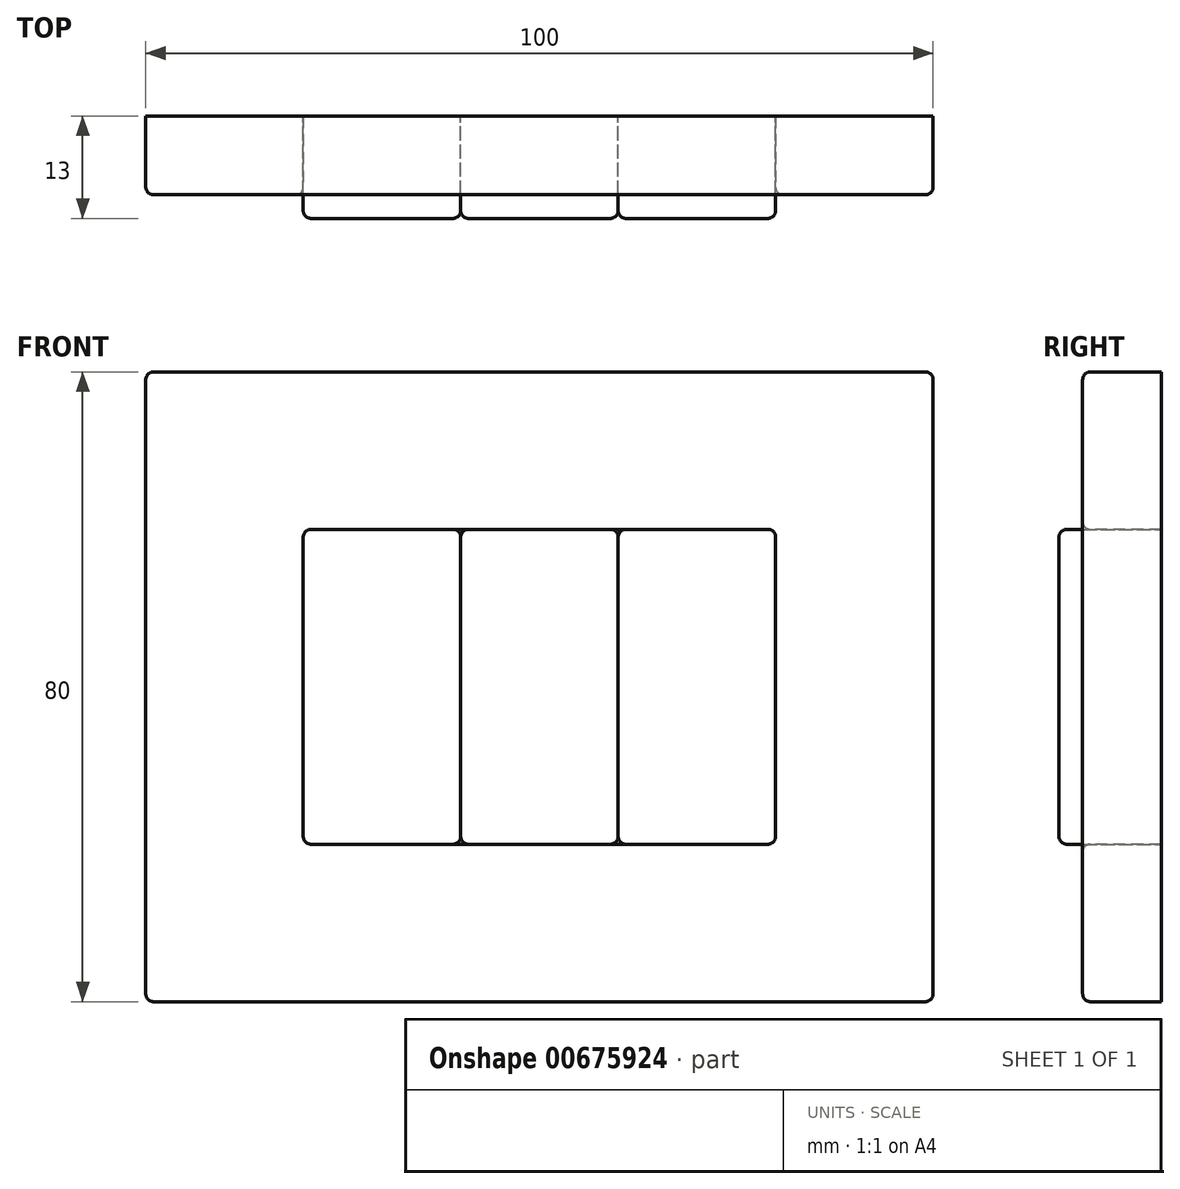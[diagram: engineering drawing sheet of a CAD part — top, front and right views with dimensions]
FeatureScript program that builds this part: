
annotation { "Feature Type Name" : "Feature", "Feature Type Description" : "" }
export const myFeature = defineFeature(function(context is Context, id is Id, definition is map)
    precondition{}
    {
        {
            var Q0;
            Q0=qCreatedBy(makeId("Front.planeOp"),FACE);
            var sketch = newSketch(context, id + "F0", { "sketchPlane" : qUnion([Q0])});
            skLineSegment(sketch, "E0.bottom", {"start": v(0, 0) * mm, "end": v(100, 0) * mm});
            skLineSegment(sketch, "E0.top", {"start": v(0, 80) * mm, "end": v(100, 80) * mm});
            skLineSegment(sketch, "E0.left", {"start": v(0, 0) * mm, "end": v(0, 80) * mm});
            skLineSegment(sketch, "E0.right", {"start": v(100, 0) * mm, "end": v(100, 80) * mm});
            skLineSegment(sketch, "E1.bottom", {"start": v(20, 60) * mm, "end": v(40, 60) * mm});
            skLineSegment(sketch, "E1.top", {"start": v(20, 20) * mm, "end": v(40, 20) * mm});
            skLineSegment(sketch, "E1.left", {"start": v(20, 60) * mm, "end": v(20, 20) * mm});
            skLineSegment(sketch, "E1.right", {"start": v(40, 60) * mm, "end": v(40, 20) * mm});
            skLineSegment(sketch, "E2.bottom", {"start": v(40, 60) * mm, "end": v(60, 60) * mm});
            skLineSegment(sketch, "E2.top", {"start": v(40, 20) * mm, "end": v(60, 20) * mm});
            skLineSegment(sketch, "E2.right", {"start": v(60, 60) * mm, "end": v(60, 20) * mm});
            skLineSegment(sketch, "E3.bottom", {"start": v(60, 60) * mm, "end": v(80, 60) * mm});
            skLineSegment(sketch, "E3.top", {"start": v(60, 20) * mm, "end": v(80, 20) * mm});
            skLineSegment(sketch, "E3.right", {"start": v(80, 60) * mm, "end": v(80, 20) * mm});
            skLineSegment(sketch, "E4", {"start": v(20, 40) * mm, "end": v(0, 40) * mm, "construction": true});
            skLineSegment(sketch, "E5", {"start": v(50, 60) * mm, "end": v(50, 80) * mm, "construction": true});
            skSolve(sketch);
        }
        {
            var Q0;
            Q0=makeQuery(id+"F0.imprint","IMPRINT",FACE,{"disambiguationData":[TD([[makeQuery(id+"F0.imprint","IMPRINT",EDGE,{"derivedFrom":sQuery(id+"F0.wireOp",EDGE,"E1.bottom")}),-1.0]])]});
            var Q1;
            Q1=makeQuery(id+"F0.imprint","IMPRINT",FACE,{"disambiguationData":[TD([[makeQuery(id+"F0.imprint","IMPRINT",EDGE,{"derivedFrom":sQuery(id+"F0.wireOp",EDGE,"E3.bottom")}),-1.0]])]});
            extrude(context, id + "F1", {"entities" : qUnion([Q0, Q1]), "depth" : 3 * mm, "offsetDistance" : 25 * mm, "hasSecondDirection" : true, "secondDirectionOppositeDirection" : true, "secondDirectionDepth" : 10 * mm});
        }
        {
            var Q0;
            Q0=makeQuery(id+"F0.imprint","IMPRINT",FACE,{"disambiguationData":[TD([[makeQuery(id+"F0.imprint","IMPRINT",EDGE,{"derivedFrom":sQuery(id+"F0.wireOp",EDGE,"E2.bottom")}),-1.0]])]});
            extrude(context, id + "F2", {"entities" : qUnion([Q0]), "depth" : 3 * mm, "offsetDistance" : 25 * mm, "hasSecondDirection" : true, "secondDirectionOppositeDirection" : true, "secondDirectionDepth" : 10 * mm});
        }
        {
            var Q0;
            Q0=makeQuery(id+"F1.opExtrude","CAP_FACE",FACE,{"disambiguationData":[OSD([sQuery(id+"F0.wireOp",EDGE,"E1.bottom"),sQuery(id+"F0.wireOp",EDGE,"E1.top"),sQuery(id+"F0.wireOp",EDGE,"E1.left"),sQuery(id+"F0.wireOp",EDGE,"E1.right")])],"isStart":false});
            var Q1;
            Q1=makeQuery(id+"F1.opExtrude","CAP_FACE",FACE,{"disambiguationData":[OSD([sQuery(id+"F0.wireOp",EDGE,"E3.bottom"),sQuery(id+"F0.wireOp",EDGE,"E3.top"),sQuery(id+"F0.wireOp",EDGE,"E2.right"),sQuery(id+"F0.wireOp",EDGE,"E3.right")])],"isStart":false});
            var Q2;
            Q2=makeQuery(id+"F1.opExtrude","SWEPT_EDGE",EDGE,{"disambiguationData":[OSD([sQuery(id+"F0.wireOp",EDGE,"E2.bottom"),sQuery(id+"F0.wireOp",EDGE,"E3.bottom"),sQuery(id+"F0.wireOp",EDGE,"E2.right")])]});
            var Q3;
            Q3=makeQuery(id+"F1.opExtrude","SWEPT_EDGE",EDGE,{"disambiguationData":[OSD([sQuery(id+"F0.wireOp",EDGE,"E3.bottom"),sQuery(id+"F0.wireOp",EDGE,"E3.right")])]});
            var Q4;
            Q4=makeQuery(id+"F1.opExtrude","SWEPT_EDGE",EDGE,{"disambiguationData":[OSD([sQuery(id+"F0.wireOp",EDGE,"E1.bottom"),sQuery(id+"F0.wireOp",EDGE,"E2.bottom"),sQuery(id+"F0.wireOp",EDGE,"E1.right")])]});
            var Q5;
            Q5=makeQuery(id+"F1.opExtrude","SWEPT_EDGE",EDGE,{"disambiguationData":[OSD([sQuery(id+"F0.wireOp",EDGE,"E1.bottom"),sQuery(id+"F0.wireOp",EDGE,"E1.left")])]});
            var Q6;
            Q6=makeQuery(id+"F1.opExtrude","SWEPT_EDGE",EDGE,{"disambiguationData":[OSD([sQuery(id+"F0.wireOp",EDGE,"E1.top"),sQuery(id+"F0.wireOp",EDGE,"E1.left")])]});
            var Q7;
            Q7=makeQuery(id+"F1.opExtrude","SWEPT_EDGE",EDGE,{"disambiguationData":[OSD([sQuery(id+"F0.wireOp",EDGE,"E1.top"),sQuery(id+"F0.wireOp",EDGE,"E2.top"),sQuery(id+"F0.wireOp",EDGE,"E1.right")])]});
            var Q8;
            Q8=makeQuery(id+"F1.opExtrude","SWEPT_EDGE",EDGE,{"disambiguationData":[OSD([sQuery(id+"F0.wireOp",EDGE,"E2.top"),sQuery(id+"F0.wireOp",EDGE,"E3.top"),sQuery(id+"F0.wireOp",EDGE,"E2.right")])]});
            var Q9;
            Q9=makeQuery(id+"F1.opExtrude","SWEPT_EDGE",EDGE,{"disambiguationData":[OSD([sQuery(id+"F0.wireOp",EDGE,"E3.top"),sQuery(id+"F0.wireOp",EDGE,"E3.right")])]});
            fillet(context, id + "F3", {"entities" : qUnion([Q0, Q1, Q2, Q3, Q4, Q5, Q6, Q7, Q8, Q9]), "radius" : 1 * mm, "tangentPropagation" : true, "allowEdgeOverflow" : false});
        }
        {
            var Q0;
            Q0=makeQuery(id+"F0.imprint","IMPRINT",FACE,{"disambiguationData":[TD([[makeQuery(id+"F0.imprint","IMPRINT",EDGE,{"derivedFrom":sQuery(id+"F0.wireOp",EDGE,"E0.bottom")}),1.0]])]});
            extrude(context, id + "F4", {"entities" : qUnion([Q0]), "oppositeDirection" : true, "depth" : 10 * mm, "offsetDistance" : 25 * mm});
        }
        {
            var Q0;
            Q0=makeQuery(id+"F2.opExtrude","CAP_FACE",FACE,{"disambiguationData":[OSD([sQuery(id+"F0.wireOp",EDGE,"E2.bottom"),sQuery(id+"F0.wireOp",EDGE,"E2.top"),sQuery(id+"F0.wireOp",EDGE,"E1.right"),sQuery(id+"F0.wireOp",EDGE,"E2.right")])],"isStart":false});
            var Q1;
            Q1=makeQuery(id+"F2.opExtrude","SWEPT_EDGE",EDGE,{"disambiguationData":[OSD([sQuery(id+"F0.wireOp",EDGE,"E1.bottom"),sQuery(id+"F0.wireOp",EDGE,"E2.bottom"),sQuery(id+"F0.wireOp",EDGE,"E1.right")])]});
            var Q2;
            Q2=makeQuery(id+"F2.opExtrude","SWEPT_EDGE",EDGE,{"disambiguationData":[OSD([sQuery(id+"F0.wireOp",EDGE,"E2.bottom"),sQuery(id+"F0.wireOp",EDGE,"E3.bottom"),sQuery(id+"F0.wireOp",EDGE,"E2.right")])]});
            var Q3;
            Q3=makeQuery(id+"F2.opExtrude","SWEPT_EDGE",EDGE,{"disambiguationData":[OSD([sQuery(id+"F0.wireOp",EDGE,"E2.top"),sQuery(id+"F0.wireOp",EDGE,"E3.top"),sQuery(id+"F0.wireOp",EDGE,"E2.right")])]});
            var Q4;
            Q4=makeQuery(id+"F2.opExtrude","SWEPT_EDGE",EDGE,{"disambiguationData":[OSD([sQuery(id+"F0.wireOp",EDGE,"E1.top"),sQuery(id+"F0.wireOp",EDGE,"E2.top"),sQuery(id+"F0.wireOp",EDGE,"E1.right")])]});
            var Q5;
            Q5=makeQuery(id+"F4.opExtrude","CAP_EDGE",EDGE,{"disambiguationData":[OSD([sQuery(id+"F0.wireOp",EDGE,"E0.top")])],"isStart":true});
            var Q6;
            Q6=makeQuery(id+"F4.opExtrude","SWEPT_EDGE",EDGE,{"disambiguationData":[OSD([sQuery(id+"F0.wireOp",EDGE,"E0.top"),sQuery(id+"F0.wireOp",EDGE,"E0.left")])]});
            var Q7;
            Q7=makeQuery(id+"F4.opExtrude","CAP_EDGE",EDGE,{"disambiguationData":[OSD([sQuery(id+"F0.wireOp",EDGE,"E0.left")])],"isStart":true});
            var Q8;
            Q8=makeQuery(id+"F4.opExtrude","CAP_EDGE",EDGE,{"disambiguationData":[OSD([sQuery(id+"F0.wireOp",EDGE,"E0.bottom")])],"isStart":true});
            var Q9;
            Q9=makeQuery(id+"F4.opExtrude","SWEPT_EDGE",EDGE,{"disambiguationData":[OSD([sQuery(id+"F0.wireOp",EDGE,"E0.bottom"),sQuery(id+"F0.wireOp",EDGE,"E0.left")])]});
            var Q10;
            Q10=makeQuery(id+"F4.opExtrude","SWEPT_EDGE",EDGE,{"disambiguationData":[OSD([sQuery(id+"F0.wireOp",EDGE,"E0.top"),sQuery(id+"F0.wireOp",EDGE,"E0.right")])]});
            var Q11;
            Q11=makeQuery(id+"F4.opExtrude","CAP_EDGE",EDGE,{"disambiguationData":[OSD([sQuery(id+"F0.wireOp",EDGE,"E0.right")])],"isStart":true});
            var Q12;
            Q12=makeQuery(id+"F4.opExtrude","SWEPT_EDGE",EDGE,{"disambiguationData":[OSD([sQuery(id+"F0.wireOp",EDGE,"E0.bottom"),sQuery(id+"F0.wireOp",EDGE,"E0.right")])]});
            var Q13;
            Q13=makeQuery(id+"F4.opExtrude","CAP_EDGE",EDGE,{"disambiguationData":[OSD([sQuery(id+"F0.wireOp",EDGE,"E1.bottom"),sQuery(id+"F0.wireOp",EDGE,"E2.bottom"),sQuery(id+"F0.wireOp",EDGE,"E3.bottom")])],"isStart":true});
            var Q14;
            Q14=makeQuery(id+"F4.opExtrude","CAP_EDGE",EDGE,{"disambiguationData":[OSD([sQuery(id+"F0.wireOp",EDGE,"E1.left")])],"isStart":true});
            var Q15;
            Q15=makeQuery(id+"F4.opExtrude","CAP_EDGE",EDGE,{"disambiguationData":[OSD([sQuery(id+"F0.wireOp",EDGE,"E3.right")])],"isStart":true});
            var Q16;
            Q16=makeQuery(id+"F4.opExtrude","CAP_EDGE",EDGE,{"disambiguationData":[OSD([sQuery(id+"F0.wireOp",EDGE,"E1.top"),sQuery(id+"F0.wireOp",EDGE,"E2.top"),sQuery(id+"F0.wireOp",EDGE,"E3.top")])],"isStart":true});
            var Q17;
            Q17=makeQuery(id+"F4.opExtrude","SWEPT_EDGE",EDGE,{"disambiguationData":[OSD([sQuery(id+"F0.wireOp",EDGE,"E3.top"),sQuery(id+"F0.wireOp",EDGE,"E3.right")])]});
            var Q18;
            Q18=makeQuery(id+"F4.opExtrude","SWEPT_EDGE",EDGE,{"disambiguationData":[OSD([sQuery(id+"F0.wireOp",EDGE,"E3.bottom"),sQuery(id+"F0.wireOp",EDGE,"E3.right")])]});
            var Q19;
            Q19=makeQuery(id+"F4.opExtrude","SWEPT_EDGE",EDGE,{"disambiguationData":[OSD([sQuery(id+"F0.wireOp",EDGE,"E1.bottom"),sQuery(id+"F0.wireOp",EDGE,"E1.left")])]});
            var Q20;
            Q20=makeQuery(id+"F4.opExtrude","SWEPT_EDGE",EDGE,{"disambiguationData":[OSD([sQuery(id+"F0.wireOp",EDGE,"E1.top"),sQuery(id+"F0.wireOp",EDGE,"E1.left")])]});
            fillet(context, id + "F5", {"entities" : qUnion([Q0, Q1, Q2, Q3, Q4, Q5, Q6, Q7, Q8, Q9, Q10, Q11, Q12, Q13, Q14, Q15, Q16, Q17, Q18, Q19, Q20]), "radius" : 1 * mm, "tangentPropagation" : true, "allowEdgeOverflow" : false});
        }
    });
